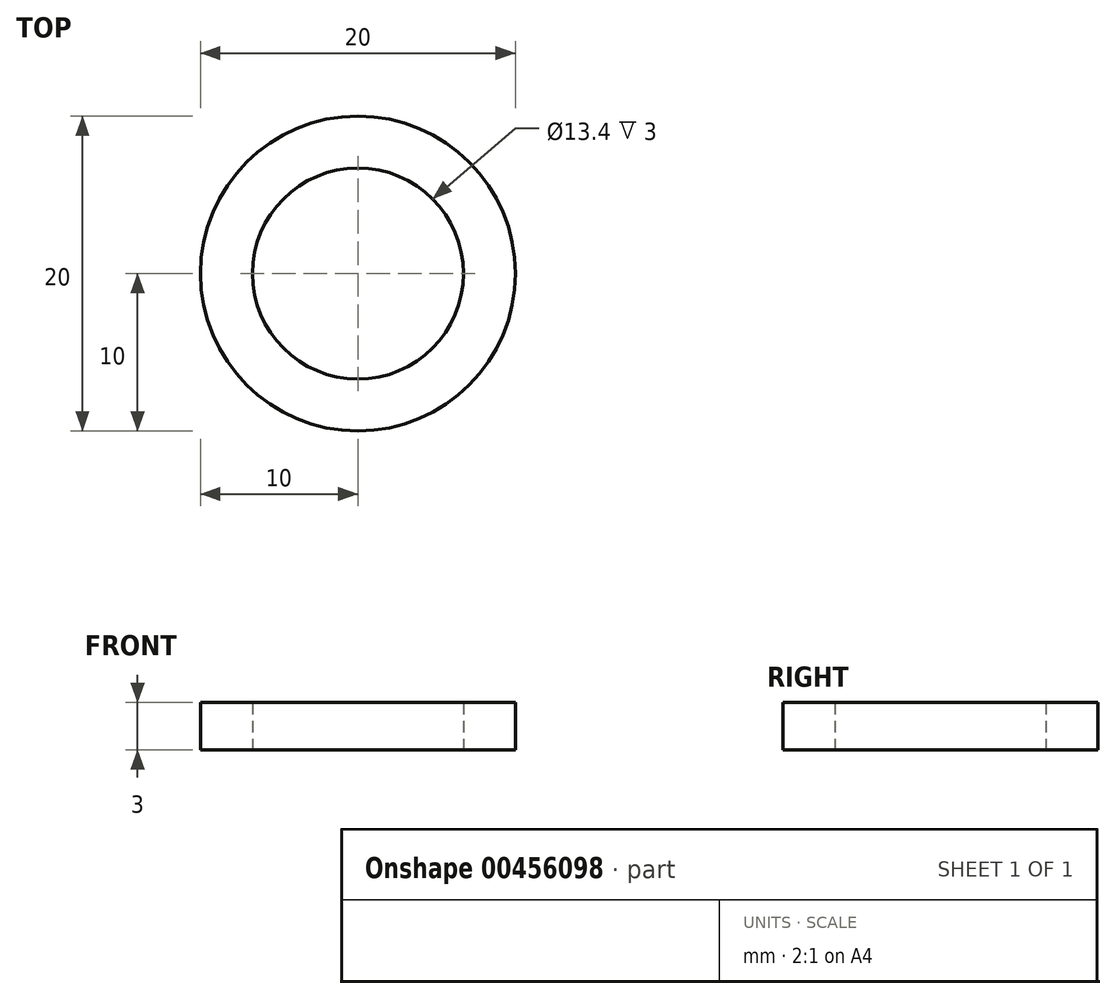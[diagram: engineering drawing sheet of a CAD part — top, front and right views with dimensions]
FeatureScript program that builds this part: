
annotation { "Feature Type Name" : "Feature", "Feature Type Description" : "" }
export const myFeature = defineFeature(function(context is Context, id is Id, definition is map)
    precondition{}
    {
        {
            var Q0;
            Q0=qCreatedBy(makeId("Top.planeOp"),FACE);
            var sketch = newSketch(context, id + "F0", { "sketchPlane" : qUnion([Q0])});
            skCircle(sketch, "E0", {"center": v(0, 0) * mm, "radius": 6.7 * mm});
            skCircle(sketch, "E1", {"center": v(0, 0) * mm, "radius": 10 * mm});
            skSolve(sketch);
        }
        {
            var Q0;
            Q0=makeQuery(id+"F0.imprint","IMPRINT",FACE,{"disambiguationData":[TD([[makeQuery(id+"F0.imprint","IMPRINT",EDGE,{"derivedFrom":sQuery(id+"F0.wireOp",EDGE,"E0")}),-1.0]])]});
            extrude(context, id + "F1", {"entities" : qUnion([Q0]), "depth" : 3 * mm});
        }
    });
